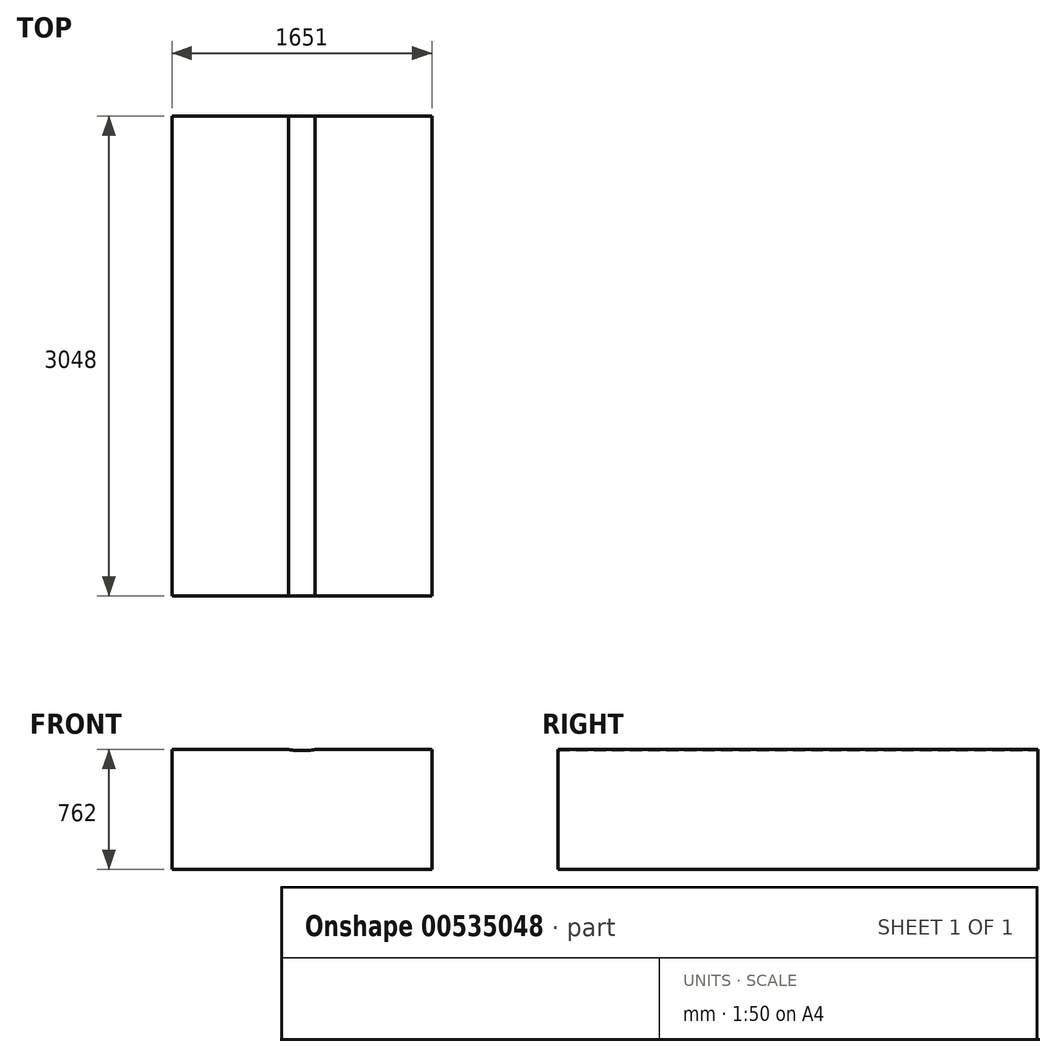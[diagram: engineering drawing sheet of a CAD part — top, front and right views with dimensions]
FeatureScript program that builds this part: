
annotation { "Feature Type Name" : "Feature", "Feature Type Description" : "" }
export const myFeature = defineFeature(function(context is Context, id is Id, definition is map)
    precondition{}
    {
        {
            var Q0;
            Q0=qCreatedBy(makeId("Front.planeOp"),FACE);
            var sketch = newSketch(context, id + "F0", { "sketchPlane" : qUnion([Q0])});
            skLineSegment(sketch, "E0.bottom", {"start": v(0, 0) * mm, "end": v(-1651, 0) * mm});
            skLineSegment(sketch, "E0.top", {"start": v(0, 762) * mm, "end": v(-1651, 762) * mm});
            skLineSegment(sketch, "E0.left", {"start": v(0, 0) * mm, "end": v(0, 762) * mm});
            skLineSegment(sketch, "E0.right", {"start": v(-1651, 0) * mm, "end": v(-1651, 762) * mm});
            skCircle(sketch, "E1", {"center": v(-825.5, 1229.65) * mm, "radius": 475.17 * mm});
            skPoint(sketch, "E1.centerSnap0", {"position": v(-825.5, 762) * mm});
            skCircle(sketch, "E2", {"center": v(-825.5, 1229.65) * mm, "radius": 418.01 * mm});
            skLineSegment(sketch, "E3.bottom", {"start": v(-832.16, 1704.77) * mm, "end": v(-790.9, 1704.77) * mm});
            skLineSegment(sketch, "E3.top", {"start": v(-832.16, 1646.23) * mm, "end": v(-790.9, 1646.23) * mm});
            skLineSegment(sketch, "E3.left", {"start": v(-832.16, 1704.77) * mm, "end": v(-832.16, 1646.23) * mm});
            skLineSegment(sketch, "E3.right", {"start": v(-790.9, 1704.77) * mm, "end": v(-790.9, 1646.23) * mm});
            skSolve(sketch);
        }
        {
            var Q0;
            {var subQ0=sQuery(id+"F0.wireOp",EDGE,"E1");var subQ1=sQuery(id+"F0.wireOp",EDGE,"E0.top");var subQ2=makeQuery(id+"F0.imprint","INTERSECT",VERTEX,{"disambiguationData":[OD(0.0)],"derivedFrom":[subQ1,subQ0]});Q0=makeQuery(id+"F0.imprint","IMPRINT",FACE,{"disambiguationData":[TD([[makeQuery(id+"F0.imprint","IMPRINT",EDGE,{"disambiguationData":[TD([[subQ2,-1.0]])],"derivedFrom":subQ1}),-1.0]])]});}
            var Q1;
            Q1=makeQuery(id+"F0.imprint","IMPRINT",FACE,{"disambiguationData":[TD([[makeQuery(id+"F0.imprint","IMPRINT",EDGE,{"derivedFrom":sQuery(id+"F0.wireOp",EDGE,"E0.bottom")}),-1.0]])]});
            extrude(context, id + "F1", {"entities" : qUnion([Q0, Q1]), "depth" : 3048 * mm, "offsetDistance" : 25.4 * mm});
        }
    });
